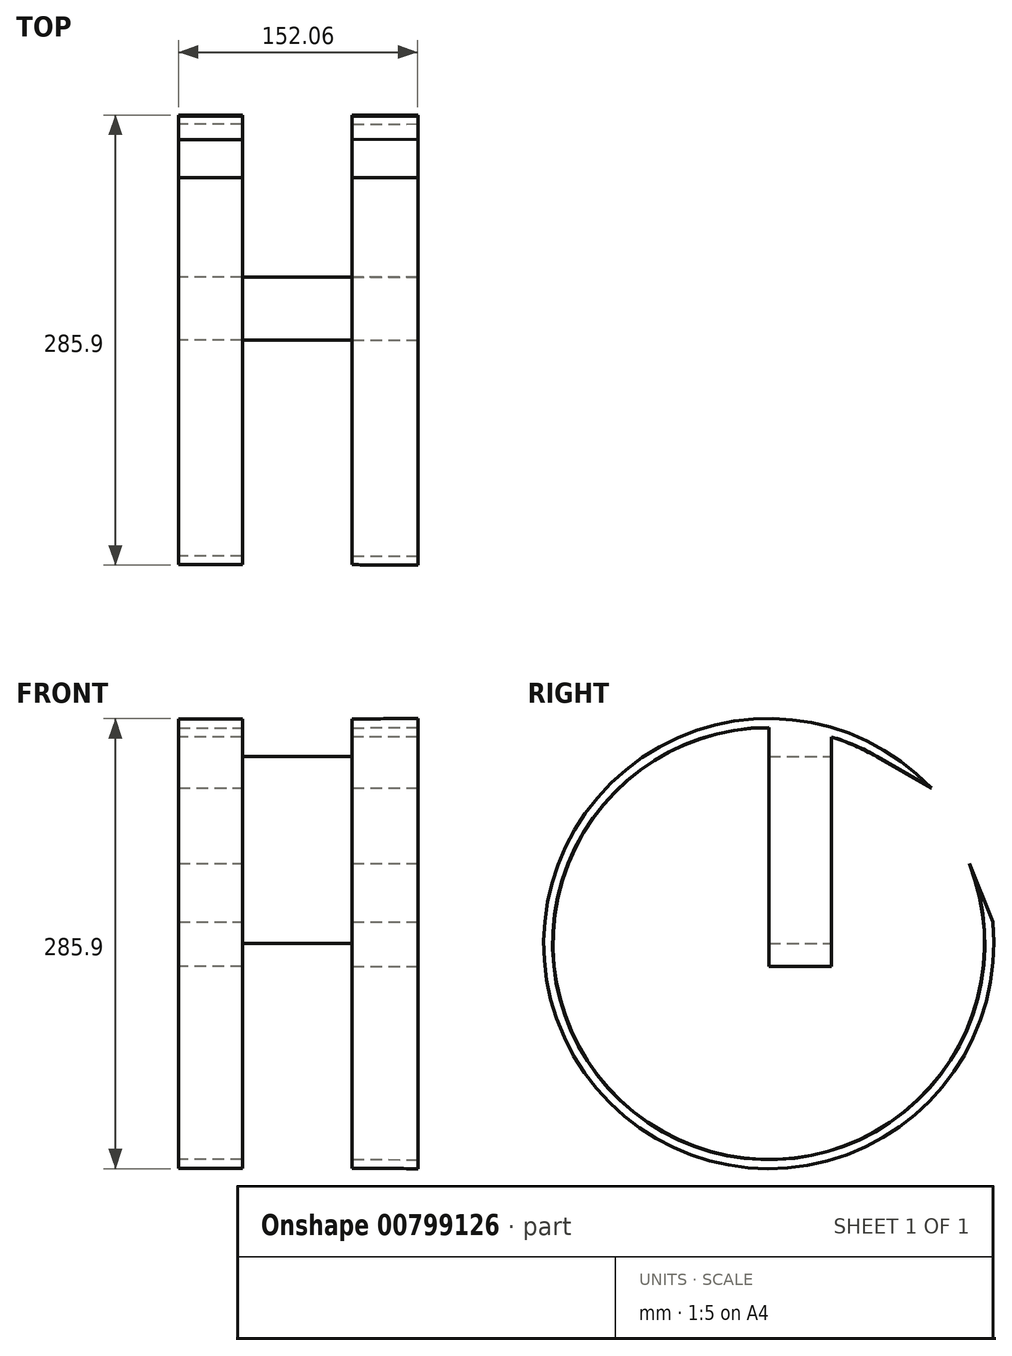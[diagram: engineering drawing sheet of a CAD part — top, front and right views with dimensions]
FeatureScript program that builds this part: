
annotation { "Feature Type Name" : "Feature", "Feature Type Description" : "" }
export const myFeature = defineFeature(function(context is Context, id is Id, definition is map)
    precondition{}
    {
        {
            var Q0;
            Q0=qCreatedBy(makeId("Front.planeOp"),FACE);
            var sketch = newSketch(context, id + "F0", { "sketchPlane" : qUnion([Q0])});
            skLineSegment(sketch, "E0", {"start": v(-76.55, 75.3) * mm, "end": v(-76.55, -76.34) * mm});
            skLineSegment(sketch, "E1", {"start": v(75.51, -76.34) * mm, "end": v(75.51, 75.51) * mm});
            skLineSegment(sketch, "E2", {"start": v(-76.55, 75.3) * mm, "end": v(-35.9, 75.3) * mm});
            skLineSegment(sketch, "E3", {"start": v(-35.9, 75.3) * mm, "end": v(-35.9, 57.25) * mm});
            skLineSegment(sketch, "E4", {"start": v(33.88, 57.25) * mm, "end": v(33.88, 75.3) * mm});
            skLineSegment(sketch, "E5", {"start": v(33.88, 75.3) * mm, "end": v(75.51, 75.51) * mm});
            skLineSegment(sketch, "E6", {"start": v(33.88, 57.25) * mm, "end": v(-35.9, 57.25) * mm});
            skLineSegment(sketch, "E7", {"start": v(-35.9, -76.34) * mm, "end": v(-35.9, -61.75) * mm});
            skPoint(sketch, "E7.startSnap0", {"position": v(-35.9, 66.28) * mm});
            skLineSegment(sketch, "E8", {"start": v(-35.9, -61.75) * mm, "end": v(33.88, -61.75) * mm});
            skLineSegment(sketch, "E9", {"start": v(33.88, -61.75) * mm, "end": v(33.88, -76.34) * mm});
            skLineSegment(sketch, "E10", {"start": v(-35.9, -76.34) * mm, "end": v(-76.55, -76.34) * mm});
            skLineSegment(sketch, "E11", {"start": v(33.88, -76.34) * mm, "end": v(75.51, -76.34) * mm});
            skSolve(sketch);
        }
        {
            var Q0;
            Q0 = qSketchRegion(id + "F0", true);
            extrude(context, id + "F1", {"entities" : qUnion([Q0]), "depth" : 25.4 * mm, "offsetDistance" : 25.4 * mm});
        }
        {
            var Q0;
            Q0=makeQuery(id+"F1.opExtrude","CAP_FACE",FACE,{"disambiguationData":[OSD([sQuery(id+"F0.wireOp",EDGE,"E0"),sQuery(id+"F0.wireOp",EDGE,"E1"),sQuery(id+"F0.wireOp",EDGE,"E2"),sQuery(id+"F0.wireOp",EDGE,"E3"),sQuery(id+"F0.wireOp",EDGE,"E4"),sQuery(id+"F0.wireOp",EDGE,"E5"),sQuery(id+"F0.wireOp",EDGE,"E6"),sQuery(id+"F0.wireOp",EDGE,"E7"),sQuery(id+"F0.wireOp",EDGE,"E8"),sQuery(id+"F0.wireOp",EDGE,"E9"),sQuery(id+"F0.wireOp",EDGE,"E10"),sQuery(id+"F0.wireOp",EDGE,"E11")])],"isStart":false});
            var sketch = newSketch(context, id + "F2", { "sketchPlane" : qUnion([Q0])});
            skSolve(sketch);
        }
        {
            var Q0;
            Q0=makeQuery(id+"F2.imprint","IMPRINT",FACE,{"disambiguationData":[TD([[makeQuery(id+"F2.imprint","IMPRINT",EDGE,{"derivedFrom":makeQuery(id+"F1.opExtrude","CAP_EDGE",EDGE,{"disambiguationData":[OSD([sQuery(id+"F0.wireOp",EDGE,"E0")])],"isStart":false})}),1.0]])]});
            var sketch = newSketch(context, id + "F3", { "sketchPlane" : qUnion([Q0])});
            skSolve(sketch);
        }
        {
            var Q0;
            Q0=makeQuery(id+"F3.imprint","IMPRINT",FACE,{"disambiguationData":[TD([[makeQuery(id+"F3.imprint","IMPRINT",EDGE,{"derivedFrom":makeQuery(id+"F2.imprint","IMPRINT",EDGE,{"derivedFrom":makeQuery(id+"F1.opExtrude","CAP_EDGE",EDGE,{"disambiguationData":[OSD([sQuery(id+"F0.wireOp",EDGE,"E0")])],"isStart":false})})}),1.0]])]});
            extrude(context, id + "F4", {"entities" : qUnion([Q0]), "operationType" : NewBodyOperationType.ADD, "depth" : 14.5 * mm, "offsetDistance" : 25.4 * mm});
        }
        {
            var Q0;
            Q0=makeQuery(id+"F4.opExtrude","CAP_FACE",FACE,{"disambiguationData":[OSD([sQuery(id+"F0.wireOp",EDGE,"E0"),sQuery(id+"F0.wireOp",EDGE,"E1"),sQuery(id+"F0.wireOp",EDGE,"E2"),sQuery(id+"F0.wireOp",EDGE,"E3"),sQuery(id+"F0.wireOp",EDGE,"E4"),sQuery(id+"F0.wireOp",EDGE,"E5"),sQuery(id+"F0.wireOp",EDGE,"E6"),sQuery(id+"F0.wireOp",EDGE,"E7"),sQuery(id+"F0.wireOp",EDGE,"E8"),sQuery(id+"F0.wireOp",EDGE,"E9"),sQuery(id+"F0.wireOp",EDGE,"E10"),sQuery(id+"F0.wireOp",EDGE,"E11")])],"isStart":false});
            var sketch = newSketch(context, id + "F5", { "sketchPlane" : qUnion([Q0])});
            skLineSegment(sketch, "E12", {"start": v(-76.55, -76.34) * mm, "end": v(-35.9, -76.34) * mm});
            skLineSegment(sketch, "E13", {"start": v(33.88, -61.75) * mm, "end": v(-35.9, -61.75) * mm});
            skLineSegment(sketch, "E14", {"start": v(75.51, -76.34) * mm, "end": v(33.88, -76.34) * mm});
            skLineSegment(sketch, "E15", {"start": v(33.88, -76.34) * mm, "end": v(33.88, -61.75) * mm});
            skLineSegment(sketch, "E16", {"start": v(-35.9, -61.75) * mm, "end": v(-35.9, -76.34) * mm});
            skSolve(sketch);
        }
        {
            var Q0;
            Q0=makeQuery(id+"F5.imprint","IMPRINT",FACE,{"disambiguationData":[TD([[makeQuery(id+"F5.imprint","IMPRINT",EDGE,{"derivedFrom":sQuery(id+"F5.wireOp",EDGE,"E12")}),-1.0]])]});
            var Q1;
            Q1=sQuery(id+"F5.wireOp",EDGE,"E14");
            var Q2;
            Q2=sQuery(id+"F5.wireOp",EDGE,"E12");
            var Q3;
            Q3=makeQuery(id+"F4.opExtrude","CAP_EDGE",EDGE,{"disambiguationData":[OSD([sQuery(id+"F0.wireOp",EDGE,"E6")])],"isStart":false});
            var Q4;
            Q4=sQuery(id+"F5.wireOp",EDGE,"E13");
            revolve(context, id + "F6", {"bodyType" : ToolBodyType.SURFACE, "operationType" : NewBodyOperationType.ADD, "surfaceOperationType" : NewSurfaceOperationType.NEW, "entities" : qUnion([Q0]), "surfaceEntities" : qUnion([Q1, Q2, Q3]), "axis" : qUnion([Q4]), "revolveType" : RevolveType.FULL});
        }
        {
            var Q0;
            {var subQ0=sQuery(id+"F0.wireOp",EDGE,"E2");Q0=makeQuery(id+"F4.boolean.opBoolean","MERGE",FACE,{"derivedFrom":[makeQuery(id+"F1.opExtrude","SWEPT_FACE",FACE,{"disambiguationData":[OSD([subQ0])]}),makeQuery(id+"F4.opExtrude","SWEPT_FACE",FACE,{"disambiguationData":[OSD([subQ0])]})]});}
            var Q1;
            {var subQ0=sQuery(id+"F0.wireOp",EDGE,"E5");Q1=makeQuery(id+"F4.boolean.opBoolean","MERGE",FACE,{"derivedFrom":[makeQuery(id+"F1.opExtrude","SWEPT_FACE",FACE,{"disambiguationData":[OSD([subQ0])]}),makeQuery(id+"F4.opExtrude","SWEPT_FACE",FACE,{"disambiguationData":[OSD([subQ0])]})]});}
            var Q2;
            Q2 = qSketchRegion(id + "FC6vghze4dcz3pU_1", true);
            var Q3;
            Q3=makeQuery(id+"F6.opRevolve","SWEPT_FACE",FACE,{"disambiguationData":[OSD([sQuery(id+"F0.wireOp",EDGE,"E6")])]});
            revolve(context, id + "F7", {"operationType" : NewBodyOperationType.ADD, "surfaceOperationType" : NewSurfaceOperationType.NEW, "entities" : qUnion([Q0, Q1, Q2]), "axis" : qUnion([Q3]), "revolveType" : RevolveType.TWO_DIRECTIONS, "angle" : 291.76 * degree, "angleBack" : 330 * degree});
        }
        {
            var Q0;
            Q0=makeQuery(id+"F6.opRevolve","SWEPT_BODY",BODY,{"disambiguationData":[OSD([sQuery(id+"F0.wireOp",EDGE,"E6")])]});
            var Q1;
            Q1=makeQuery(id+"F6.opRevolve","SWEPT_BODY",BODY,{"disambiguationData":[OSD([sQuery(id+"F5.wireOp",EDGE,"E12")])]});
            deleteBodies(context, id + "F8", {"entities" : qUnion([Q0, Q1])});
        }
        {
            var Q0;
            Q0=makeQuery(id+"F6.opRevolve","SWEPT_BODY",BODY,{"disambiguationData":[OSD([sQuery(id+"F5.wireOp",EDGE,"E14")])]});
            deleteBodies(context, id + "F9", {"entities" : qUnion([Q0])});
        }
    });
